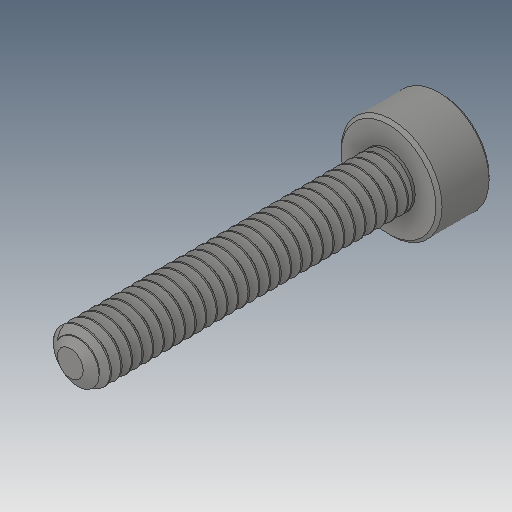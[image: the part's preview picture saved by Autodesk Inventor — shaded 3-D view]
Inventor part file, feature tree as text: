
AUTODESK INVENTOR PART (.ipt)
format: ipt  version: 2019 (Build 230136000, 136)  size: 916,480 bytes
history: native  units: in
note: dims shown in document units (in); Inventor stores cm internally (conversion verified against a paired STEP export)
features: revolve x1
ambient origin geometry x8: Origin, YZ Plane, XZ Plane, XY Plane, X Axis, Y Axis, Z Axis, Center Point
bodies: Solid1 (feature_tree)
feature tree (1):
  revolve  "Revolve1"  [1 undecoded]
note: 1 required parameter value undecoded (feature->parameter linkage not recoverable at this tier; creation-order binding heuristic only, values carry confidence <= 0.55)
